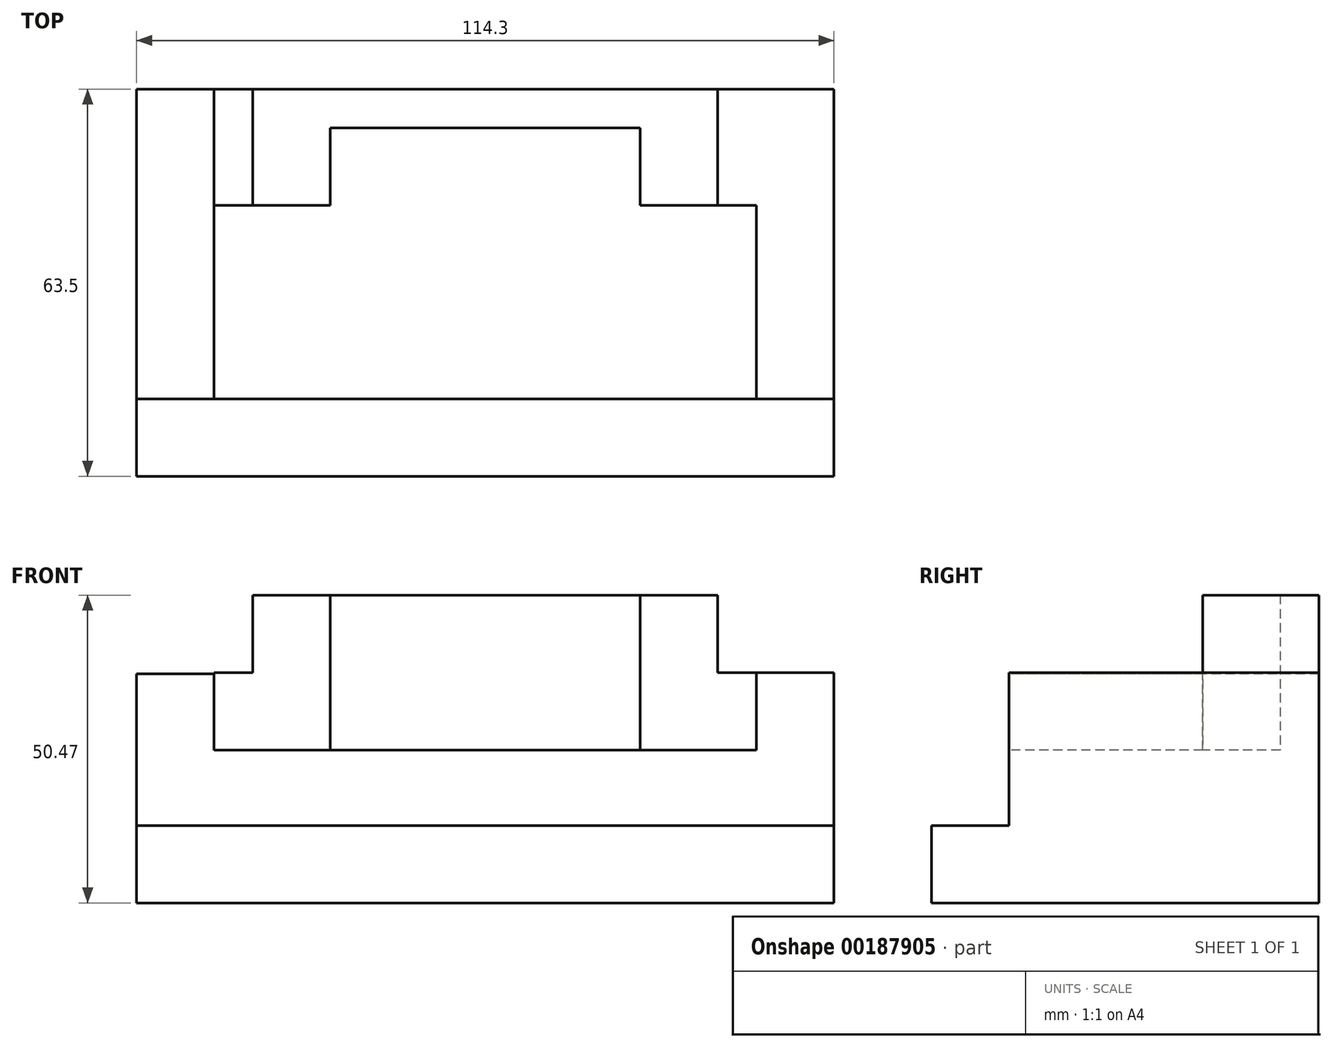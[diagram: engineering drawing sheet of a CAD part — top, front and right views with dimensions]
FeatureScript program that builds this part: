
annotation { "Feature Type Name" : "Feature", "Feature Type Description" : "" }
export const myFeature = defineFeature(function(context is Context, id is Id, definition is map)
    precondition{}
    {
        {
            var Q0;
            Q0=qCreatedBy(makeId("Right.planeOp"),FACE);
            var sketch = newSketch(context, id + "F0", { "sketchPlane" : qUnion([Q0])});
            skLineSegment(sketch, "E0.bottom", {"start": v(0, 0) * mm, "end": v(-63.5, 0) * mm});
            skLineSegment(sketch, "E0.top", {"start": v(0, 12.7) * mm, "end": v(-63.5, 12.7) * mm});
            skLineSegment(sketch, "E0.left", {"start": v(0, 0) * mm, "end": v(0, 12.7) * mm});
            skLineSegment(sketch, "E0.right", {"start": v(-63.5, 0) * mm, "end": v(-63.5, 12.7) * mm});
            skSolve(sketch);
        }
        {
            var Q0;
            Q0 = qSketchRegion(id + "F0", true);
            extrude(context, id + "F1", {"entities" : qUnion([Q0]), "depth" : 114.3 * mm});
        }
        {
            var Q0;
            Q0=qCreatedBy(makeId("Right.planeOp"),FACE);
            var sketch = newSketch(context, id + "F2", { "sketchPlane" : qUnion([Q0])});
            skLineSegment(sketch, "E1.bottom", {"start": v(0, 12.37) * mm, "end": v(-50.8, 12.37) * mm});
            skLineSegment(sketch, "E1.top", {"start": v(0, 25.07) * mm, "end": v(-50.8, 25.07) * mm});
            skLineSegment(sketch, "E1.left", {"start": v(0, 12.37) * mm, "end": v(0, 25.07) * mm});
            skLineSegment(sketch, "E1.right", {"start": v(-50.8, 12.37) * mm, "end": v(-50.8, 25.07) * mm});
            skSolve(sketch);
        }
        {
            var Q0;
            Q0 = qSketchRegion(id + "F2", true);
            extrude(context, id + "F3", {"entities" : qUnion([Q0]), "operationType" : NewBodyOperationType.ADD, "depth" : 114.3 * mm});
        }
        {
            var Q0;
            Q0=makeQuery(id+"F3.opExtrude","SWEPT_FACE",FACE,{"disambiguationData":[OSD([sQuery(id+"F2.wireOp",EDGE,"E1.right")])]});
            cPlane(context, id + "F4", {"entities" : qUnion([Q0]), "cplaneType" : CPlaneType.OFFSET, "offset" : 31.75 * mm, "oppositeDirection" : true, "width" : 152.4 * mm, "height" : 152.4 * mm});
        }
        {
            var Q0;
            Q0=makeQuery(id+"F3.opExtrude","SWEPT_FACE",FACE,{"disambiguationData":[OSD([sQuery(id+"F2.wireOp",EDGE,"E1.right")])]});
            cPlane(context, id + "F5", {"entities" : qUnion([Q0]), "cplaneType" : CPlaneType.OFFSET, "offset" : 0 * mm, "width" : 152.4 * mm, "height" : 152.4 * mm});
        }
        {
            var Q0;
            Q0=qCreatedBy(id+"F5.planeOp",FACE);
            var sketch = newSketch(context, id + "F6", { "sketchPlane" : qUnion([Q0])});
            skLineSegment(sketch, "E2.bottom", {"start": v(0, 24.89) * mm, "end": v(12.7, 24.89) * mm});
            skLineSegment(sketch, "E2.top", {"start": v(0, 37.59) * mm, "end": v(12.7, 37.59) * mm});
            skLineSegment(sketch, "E2.left", {"start": v(0, 24.89) * mm, "end": v(0, 37.59) * mm});
            skLineSegment(sketch, "E2.right", {"start": v(12.7, 24.89) * mm, "end": v(12.7, 37.59) * mm});
            skSolve(sketch);
        }
        {
            var Q0;
            Q0 = qSketchRegion(id + "F6", true);
            extrude(context, id + "F7", {"entities" : qUnion([Q0]), "operationType" : NewBodyOperationType.ADD, "oppositeDirection" : true, "depth" : 50.8 * mm});
        }
        {
            var Q0;
            Q0=makeQuery(id+"F7.boolean.opBoolean","MERGE",FACE,{"derivedFrom":[makeQuery(id+"F3.opExtrude","SWEPT_FACE",FACE,{"disambiguationData":[OSD([sQuery(id+"F2.wireOp",EDGE,"E1.right")])]}),makeQuery(id+"F7.opExtrude","CAP_FACE",FACE,{"disambiguationData":[OSD([sQuery(id+"F6.wireOp",EDGE,"E2.bottom"),sQuery(id+"F6.wireOp",EDGE,"E2.top"),sQuery(id+"F6.wireOp",EDGE,"E2.left"),sQuery(id+"F6.wireOp",EDGE,"E2.right")])],"isStart":true})]});
            var sketch = newSketch(context, id + "F8", { "sketchPlane" : qUnion([Q0])});
            skLineSegment(sketch, "E3.bottom", {"start": v(114.3, 25.07) * mm, "end": v(101.6, 25.07) * mm});
            skLineSegment(sketch, "E3.top", {"start": v(114.3, 37.77) * mm, "end": v(101.6, 37.77) * mm});
            skLineSegment(sketch, "E3.left", {"start": v(114.3, 25.07) * mm, "end": v(114.3, 37.77) * mm});
            skLineSegment(sketch, "E3.right", {"start": v(101.6, 25.07) * mm, "end": v(101.6, 37.77) * mm});
            skSolve(sketch);
        }
        {
            var Q0;
            Q0 = qSketchRegion(id + "F8", true);
            extrude(context, id + "F9", {"entities" : qUnion([Q0]), "operationType" : NewBodyOperationType.ADD, "oppositeDirection" : true, "depth" : 50.8 * mm});
        }
        {
            var Q0;
            Q0=makeQuery(id+"F9.boolean.opBoolean","MERGE",FACE,{"derivedFrom":[makeQuery(id+"F7.boolean.opBoolean","MERGE",FACE,{"derivedFrom":[makeQuery(id+"F3.boolean.opBoolean","MERGE",FACE,{"derivedFrom":[makeQuery(id+"F1.opExtrude","SWEPT_FACE",FACE,{"disambiguationData":[OSD([sQuery(id+"F0.wireOp",EDGE,"E0.left")])]}),makeQuery(id+"F3.opExtrude","SWEPT_FACE",FACE,{"disambiguationData":[OSD([sQuery(id+"F2.wireOp",EDGE,"E1.left")])]})]}),makeQuery(id+"F7.opExtrude","CAP_FACE",FACE,{"disambiguationData":[OSD([sQuery(id+"F6.wireOp",EDGE,"E2.bottom"),sQuery(id+"F6.wireOp",EDGE,"E2.top"),sQuery(id+"F6.wireOp",EDGE,"E2.left"),sQuery(id+"F6.wireOp",EDGE,"E2.right")])],"isStart":false})]}),makeQuery(id+"F9.opExtrude","CAP_FACE",FACE,{"disambiguationData":[OSD([sQuery(id+"F8.wireOp",EDGE,"E3.bottom"),sQuery(id+"F8.wireOp",EDGE,"E3.top"),sQuery(id+"F8.wireOp",EDGE,"E3.left"),sQuery(id+"F8.wireOp",EDGE,"E3.right")])],"isStart":false})]});
            var sketch = newSketch(context, id + "F10", { "sketchPlane" : qUnion([Q0])});
            skLineSegment(sketch, "E4", {"start": v(-57.15, 25.07) * mm, "end": v(-57.15, 39.84) * mm});
            skPoint(sketch, "E4.endSnap0", {"position": v(-57.15, 25.07) * mm});
            skLineSegment(sketch, "E5.bottom", {"start": v(-101.6, 25.07) * mm, "end": v(-95.25, 25.07) * mm});
            skLineSegment(sketch, "E5.top", {"start": v(-101.6, 37.77) * mm, "end": v(-95.25, 37.77) * mm});
            skLineSegment(sketch, "E5.left", {"start": v(-101.6, 25.07) * mm, "end": v(-101.6, 37.77) * mm});
            skLineSegment(sketch, "E5.right", {"start": v(-95.25, 25.07) * mm, "end": v(-95.25, 37.77) * mm});
            skLineSegment(sketch, "E6.MirrorCS", {"start": v(-12.7, 37.77) * mm, "end": v(-19.05, 37.77) * mm});
            skLineSegment(sketch, "E7.MirrorCS", {"start": v(-19.05, 25.07) * mm, "end": v(-19.05, 37.77) * mm});
            skLineSegment(sketch, "E8.MirrorCS", {"start": v(-12.7, 25.07) * mm, "end": v(-19.05, 25.07) * mm});
            skLineSegment(sketch, "E9", {"start": v(-12.7, 37.77) * mm, "end": v(-12.7, 25.07) * mm});
            skSolve(sketch);
        }
        {
            var Q0;
            Q0 = qSketchRegion(id + "F10", true);
            extrude(context, id + "F11", {"entities" : qUnion([Q0]), "operationType" : NewBodyOperationType.ADD, "oppositeDirection" : true, "depth" : 19.05 * mm});
        }
        {
            var Q0;
            Q0 = qSketchRegion(id + "F10", true);
            extrude(context, id + "F12", {"entities" : qUnion([Q0]), "operationType" : NewBodyOperationType.ADD, "oppositeDirection" : true, "depth" : 19.05 * mm});
        }
        {
            var Q0;
            Q0=makeQuery(id+"F3.opExtrude","SWEPT_FACE",FACE,{"disambiguationData":[OSD([sQuery(id+"F2.wireOp",EDGE,"E1.top")])]});
            var sketch = newSketch(context, id + "F13", { "sketchPlane" : qUnion([Q0])});
            skLineSegment(sketch, "E10.bottom", {"start": v(19.05, 0) * mm, "end": v(31.75, 0) * mm});
            skLineSegment(sketch, "E10.top", {"start": v(19.05, -19.05) * mm, "end": v(31.75, -19.05) * mm});
            skLineSegment(sketch, "E10.left", {"start": v(19.05, 0) * mm, "end": v(19.05, -19.05) * mm});
            skLineSegment(sketch, "E10.right", {"start": v(31.75, 0) * mm, "end": v(31.75, -19.05) * mm});
            skLineSegment(sketch, "E11.bottom", {"start": v(31.75, 0) * mm, "end": v(82.55, 0) * mm});
            skLineSegment(sketch, "E11.top", {"start": v(31.75, -6.35) * mm, "end": v(82.55, -6.35) * mm});
            skLineSegment(sketch, "E11.left", {"start": v(31.75, 0) * mm, "end": v(31.75, -6.35) * mm});
            skLineSegment(sketch, "E11.right", {"start": v(82.55, 0) * mm, "end": v(82.55, -6.35) * mm});
            skLineSegment(sketch, "E12.bottom", {"start": v(82.55, 0) * mm, "end": v(95.25, 0) * mm});
            skLineSegment(sketch, "E12.top", {"start": v(82.55, -19.05) * mm, "end": v(95.25, -19.05) * mm});
            skLineSegment(sketch, "E12.left", {"start": v(82.55, 0) * mm, "end": v(82.55, -19.05) * mm});
            skLineSegment(sketch, "E12.right", {"start": v(95.25, 0) * mm, "end": v(95.25, -19.05) * mm});
            skSolve(sketch);
        }
        {
            var Q0;
            Q0 = qSketchRegion(id + "F13", true);
            extrude(context, id + "F14", {"entities" : qUnion([Q0]), "operationType" : NewBodyOperationType.ADD, "depth" : 25.4 * mm});
        }
    });
